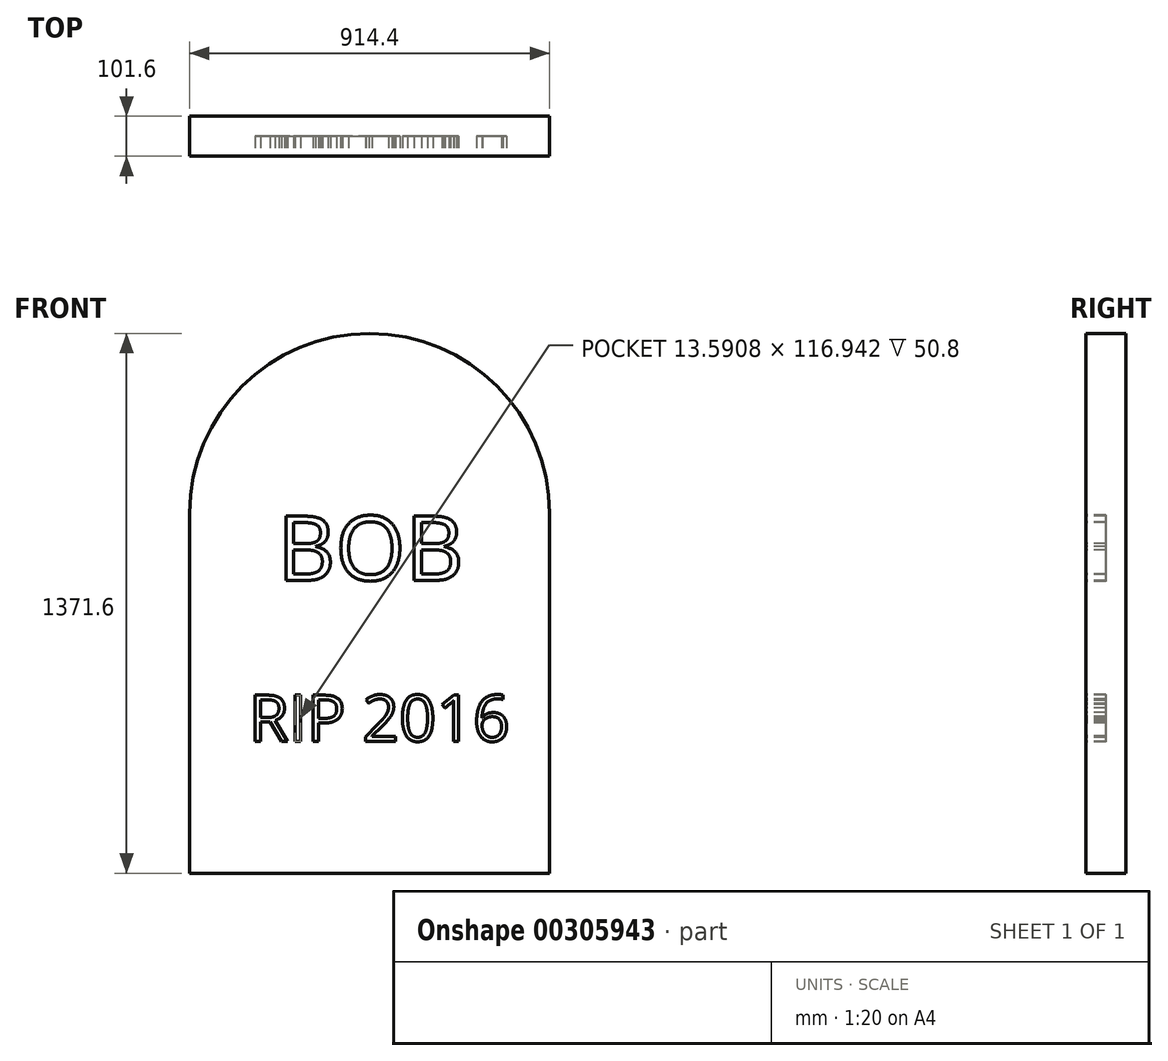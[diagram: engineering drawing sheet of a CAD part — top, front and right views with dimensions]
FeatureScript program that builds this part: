
annotation { "Feature Type Name" : "Feature", "Feature Type Description" : "" }
export const myFeature = defineFeature(function(context is Context, id is Id, definition is map)
    precondition{}
    {
        {
            var Q0;
            Q0=qCreatedBy(makeId("Front.planeOp"),FACE);
            var sketch = newSketch(context, id + "F0", { "sketchPlane" : qUnion([Q0])});
            skLineSegment(sketch, "E0.bottom", {"start": v(-902.74, 919) * mm, "end": v(11.66, 919) * mm});
            skLineSegment(sketch, "E0.top", {"start": v(-902.74, 4.6) * mm, "end": v(11.66, 4.6) * mm});
            skLineSegment(sketch, "E0.left", {"start": v(-902.74, 919) * mm, "end": v(-902.74, 4.6) * mm});
            skLineSegment(sketch, "E0.right", {"start": v(11.66, 919) * mm, "end": v(11.66, 4.6) * mm});
            skArc(sketch, "E1", {"start": v(11.66, 919) * mm, "mid": v(-445.54, 1376.2) * mm, "end": v(-902.74, 919) * mm});
            skSolve(sketch);
        }
        {
            var Q0;
            Q0=makeQuery(id+"F0.imprint","IMPRINT",FACE,{"disambiguationData":[TD([[makeQuery(id+"F0.imprint","IMPRINT",EDGE,{"derivedFrom":sQuery(id+"F0.wireOp",EDGE,"E0.bottom")}),1.0]])]});
            var Q1;
            Q1=makeQuery(id+"F0.imprint","IMPRINT",FACE,{"disambiguationData":[TD([[makeQuery(id+"F0.imprint","IMPRINT",EDGE,{"derivedFrom":sQuery(id+"F0.wireOp",EDGE,"E0.bottom")}),-1.0]])]});
            extrude(context, id + "F1", {"entities" : qUnion([Q0, Q1]), "depth" : 101.6 * mm});
        }
        {
            var Q0;
            Q0=makeQuery(id+"F1.opExtrude","CAP_FACE",FACE,{"disambiguationData":[OSD([sQuery(id+"F0.wireOp",EDGE,"E0.top"),sQuery(id+"F0.wireOp",EDGE,"E0.left"),sQuery(id+"F0.wireOp",EDGE,"E0.right"),sQuery(id+"F0.wireOp",EDGE,"E1")])],"isStart":false});
            var sketch = newSketch(context, id + "F2", { "sketchPlane" : qUnion([Q0])});
            skText(sketch, "E2", { "text": "BOB", "fontName": "OpenSans-Regular.ttf"});
            skText(sketch, "E3", { "text": "RIP 2016", "fontName": "OpenSans-Regular.ttf"});
            const initialGuessF2  = {"E2": [-0.6807, 0.74875, 1, 0, 0.16457], "E3": [-0.75201, 0.34006, 1, 0, 0.11794]};
            skSetInitialGuess(sketch, initialGuessF2);
            skSolve(sketch);
        }
        {
            var Q0;
            Q0 = qSketchRegion(id + "F2", true);
            extrude(context, id + "F3", {"entities" : qUnion([Q0]), "operationType" : NewBodyOperationType.REMOVE, "oppositeDirection" : true, "depth" : 50.8 * mm});
        }
    });
